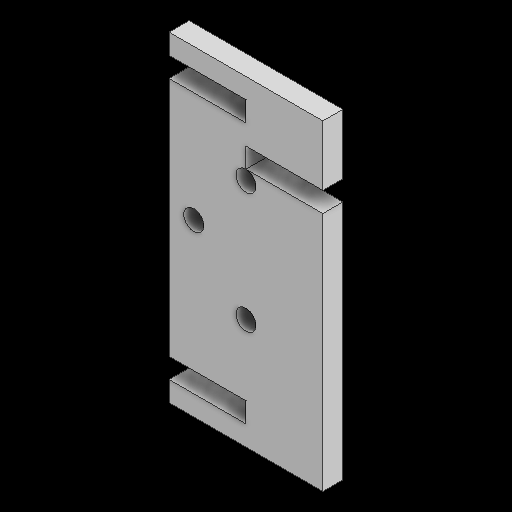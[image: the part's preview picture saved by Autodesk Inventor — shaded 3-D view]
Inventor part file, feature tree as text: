
AUTODESK INVENTOR PART (.ipt)
format: ipt  version: 2025.2 (Build 292293000, 293)  size: 110,592 bytes
history: native  units: in
note: dims shown in document units (in); Inventor stores cm internally (conversion verified against a paired STEP export)
features: extrude x1, sketch x1
ambient origin geometry x8: Origin, YZ Plane, XZ Plane, XY Plane, X Axis, Y Axis, Z Axis, Center Point
bodies: Solid1 (feature_tree)
feature tree (2):
  extrude  "Extrusion1"  [1 undecoded]
  sketch  "Sketch2"  dims[d0=0.1181in d1=0.0in]
note: 1 required parameter value undecoded (feature->parameter linkage not recoverable at this tier; creation-order binding heuristic only, values carry confidence <= 0.55)
